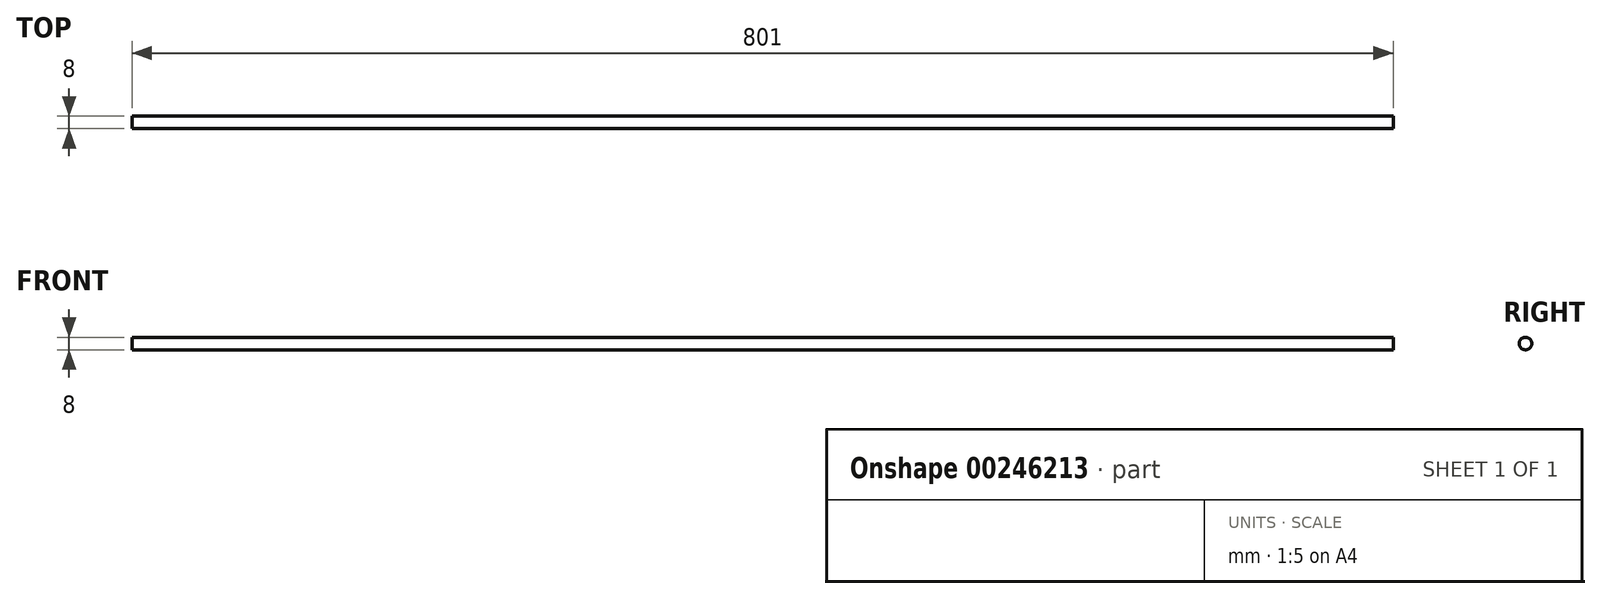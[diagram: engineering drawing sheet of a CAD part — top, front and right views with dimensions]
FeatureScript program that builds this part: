
annotation { "Feature Type Name" : "Feature", "Feature Type Description" : "" }
export const myFeature = defineFeature(function(context is Context, id is Id, definition is map)
    precondition{}
    {
        {
            var Q0;
            Q0=qCreatedBy(makeId("Front.planeOp"),FACE);
            var sketch = newSketch(context, id + "F0", { "sketchPlane" : qUnion([Q0])});
            skLineSegment(sketch, "E0.bottom", {"start": v(-394.7, 39.62) * mm, "end": v(406.3, 39.62) * mm});
            skLineSegment(sketch, "E0.top", {"start": v(-394.7, 35.62) * mm, "end": v(406.3, 35.62) * mm});
            skLineSegment(sketch, "E0.left", {"start": v(-394.7, 39.62) * mm, "end": v(-394.7, 35.62) * mm});
            skLineSegment(sketch, "E0.right", {"start": v(406.3, 39.62) * mm, "end": v(406.3, 35.62) * mm});
            skSolve(sketch);
        }
        {
            var Q0;
            Q0=makeQuery(id+"F0.imprint","IMPRINT",FACE,{"disambiguationData":[TD([[makeQuery(id+"F0.imprint","IMPRINT",EDGE,{"derivedFrom":sQuery(id+"F0.wireOp",EDGE,"E0.bottom")}),-1.0]])]});
            var Q1;
            Q1=sQuery(id+"F0.wireOp",EDGE,"E0.top");
            revolve(context, id + "F1", {"entities" : qUnion([Q0]), "axis" : qUnion([Q1]), "revolveType" : RevolveType.FULL, "oppositeDirection" : true});
        }
    });
